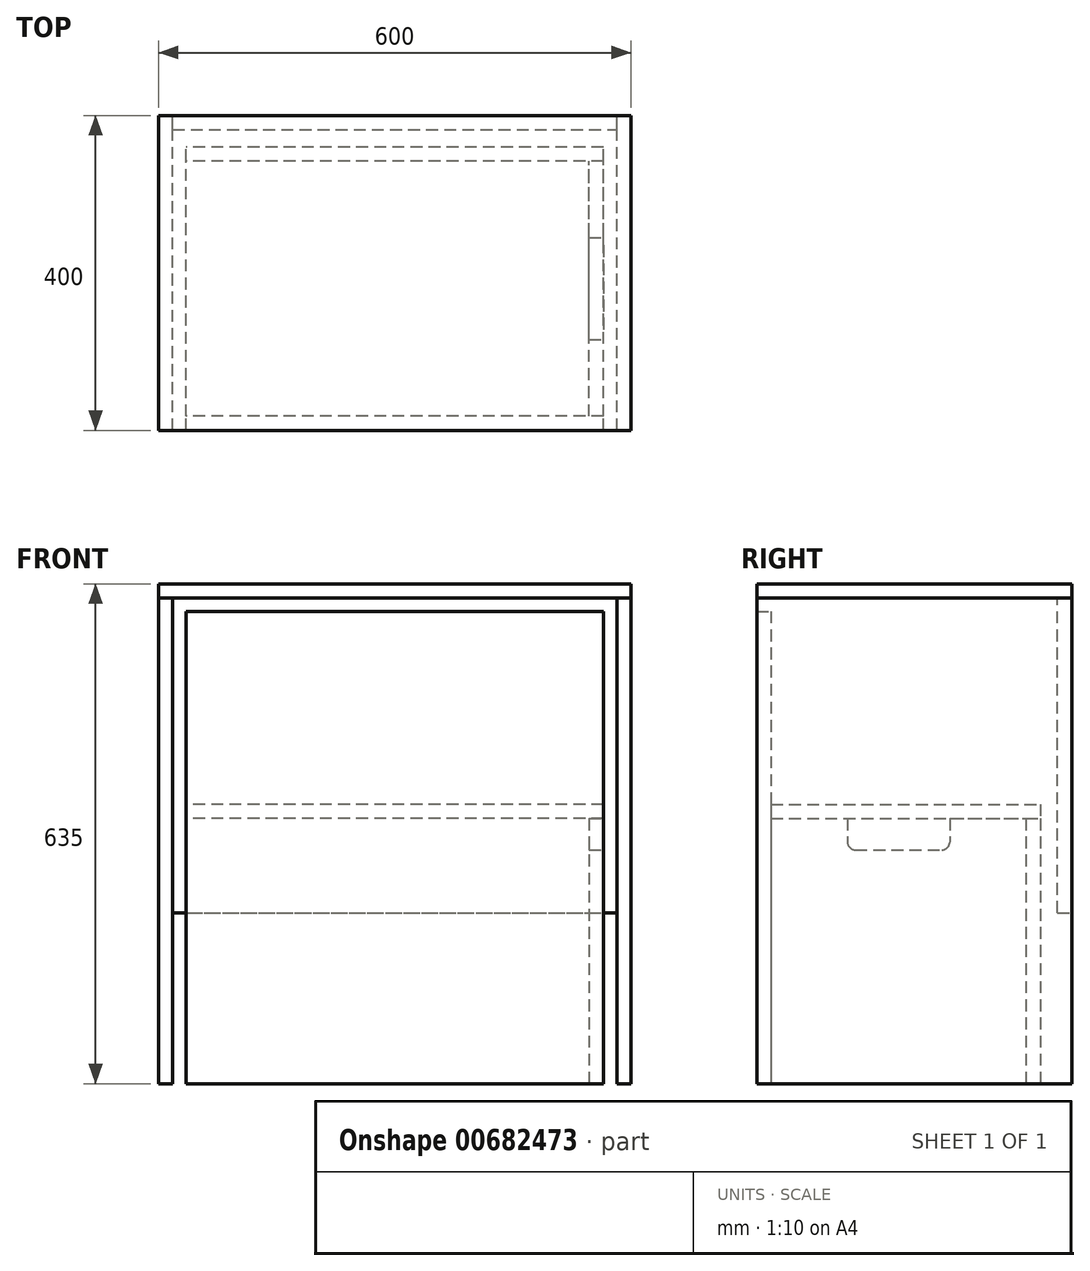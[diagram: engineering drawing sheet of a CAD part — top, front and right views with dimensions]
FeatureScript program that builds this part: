
annotation { "Feature Type Name" : "Feature", "Feature Type Description" : "" }
export const myFeature = defineFeature(function(context is Context, id is Id, definition is map)
    precondition{}
    {
        {
            var Q0;
            Q0=qCreatedBy(makeId("Front.planeOp"),FACE);
            var sketch = newSketch(context, id + "F0", { "sketchPlane" : qUnion([Q0])});
            skLineSegment(sketch, "E0.bottom", {"start": v(282, 0) * mm, "end": v(300, 0) * mm});
            skLineSegment(sketch, "E0.top", {"start": v(282, 617) * mm, "end": v(300, 617) * mm});
            skLineSegment(sketch, "E0.left", {"start": v(282, 0) * mm, "end": v(282, 617) * mm});
            skLineSegment(sketch, "E0.right", {"start": v(300, 0) * mm, "end": v(300, 617) * mm});
            skLineSegment(sketch, "E1.MirrorCS", {"start": v(-282, 0) * mm, "end": v(-282, 617) * mm});
            skLineSegment(sketch, "E2.MirrorCS", {"start": v(-282, 0) * mm, "end": v(-300, 0) * mm});
            skLineSegment(sketch, "E3.MirrorCS", {"start": v(-282, 617) * mm, "end": v(-300, 617) * mm});
            skLineSegment(sketch, "E4.MirrorCS", {"start": v(-300, 0) * mm, "end": v(-300, 617) * mm});
            skLineSegment(sketch, "E5.bottom", {"start": v(300, 617) * mm, "end": v(-300, 617) * mm});
            skLineSegment(sketch, "E5.top", {"start": v(300, 635) * mm, "end": v(-300, 635) * mm});
            skLineSegment(sketch, "E5.left", {"start": v(300, 617) * mm, "end": v(300, 635) * mm});
            skLineSegment(sketch, "E5.right", {"start": v(-300, 617) * mm, "end": v(-300, 635) * mm});
            skLineSegment(sketch, "E6", {"start": v(-282, 217) * mm, "end": v(282, 217) * mm});
            skSolve(sketch);
        }
        {
            var Q0;
            {var subQ1=sQuery(id+"F0.wireOp",EDGE,"E2.MirrorCS");Q0=makeQuery(id+"F0.imprint","IMPRINT",FACE,{"disambiguationData":[TD([[makeQuery(id+"F0.imprint","IMPRINT",EDGE,{"derivedFrom":subQ1}),-1.0]])]});}
            extrude(context, id + "F1", {"entities" : qUnion([Q0]), "depth" : 400 * mm, "offsetDistance" : 25 * mm});
        }
        {
            var Q0;
            {var subQ5=sQuery(id+"F0.wireOp",EDGE,"E0.bottom");Q0=makeQuery(id+"F0.imprint","IMPRINT",FACE,{"disambiguationData":[TD([[makeQuery(id+"F0.imprint","IMPRINT",EDGE,{"derivedFrom":subQ5}),1.0]])]});}
            extrude(context, id + "F2", {"entities" : qUnion([Q0]), "depth" : 400 * mm, "offsetDistance" : 25 * mm});
        }
        {
            var Q0;
            Q0=makeQuery(id+"F0.imprint","IMPRINT",FACE,{"disambiguationData":[TD([[makeQuery(id+"F0.imprint","IMPRINT",EDGE,{"derivedFrom":sQuery(id+"F0.wireOp",EDGE,"E5.top")}),1.0]])]});
            extrude(context, id + "F3", {"entities" : qUnion([Q0]), "depth" : 400 * mm, "offsetDistance" : 25 * mm});
        }
        {
            var Q0;
            {var subQ3=sQuery(id+"F0.wireOp",EDGE,"E6");Q0=makeQuery(id+"F0.imprint","IMPRINT",FACE,{"disambiguationData":[TD([[makeQuery(id+"F0.imprint","IMPRINT",EDGE,{"derivedFrom":subQ3}),1.0]])]});}
            extrude(context, id + "F4", {"entities" : qUnion([Q0]), "depth" : 18 * mm, "offsetDistance" : 25 * mm});
        }
        {
            var Q0;
            Q0=qCreatedBy(makeId("Right.planeOp"),FACE);
            var sketch = newSketch(context, id + "F5", { "sketchPlane" : qUnion([Q0])});
            skLineSegment(sketch, "E7.bottom", {"start": v(-400, 600) * mm, "end": v(-40, 600) * mm});
            skLineSegment(sketch, "E7.top", {"start": v(-400, 0) * mm, "end": v(-40, 0) * mm});
            skLineSegment(sketch, "E7.left", {"start": v(-400, 600) * mm, "end": v(-400, 0) * mm});
            skLineSegment(sketch, "E7.right", {"start": v(-40, 600) * mm, "end": v(-40, 0) * mm});
            skLineSegment(sketch, "E8", {"start": v(-382, 600) * mm, "end": v(-382, 0) * mm});
            skLineSegment(sketch, "E9.bottom", {"start": v(-382, 355) * mm, "end": v(-40, 355) * mm});
            skLineSegment(sketch, "E9.top", {"start": v(-382, 337) * mm, "end": v(-40, 337) * mm});
            skLineSegment(sketch, "E9.left", {"start": v(-382, 355) * mm, "end": v(-382, 337) * mm});
            skLineSegment(sketch, "E9.right", {"start": v(-40, 355) * mm, "end": v(-40, 337) * mm});
            skLineSegment(sketch, "E10", {"start": v(-58, 337) * mm, "end": v(-58, 0) * mm});
            skLineSegment(sketch, "E11", {"start": v(-364, 337) * mm, "end": v(-364, 287) * mm});
            skLineSegment(sketch, "E12", {"start": v(-364, 287) * mm, "end": v(-382, 287) * mm});
            skSolve(sketch);
        }
        {
            var Q0;
            {var subQ4=sQuery(id+"F5.wireOp",EDGE,"E7.left");Q0=makeQuery(id+"F5.imprint","IMPRINT",FACE,{"disambiguationData":[TD([[makeQuery(id+"F5.imprint","IMPRINT",EDGE,{"derivedFrom":subQ4}),1.0]])]});}
            extrude(context, id + "F6", {"entities" : qUnion([Q0]), "endBound" : BoundingType.SYMMETRIC, "depth" : 530 * mm, "offsetDistance" : 25 * mm});
        }
        {
            var Q0;
            Q0=makeQuery(id+"F5.imprint","IMPRINT",FACE,{"disambiguationData":[TD([[makeQuery(id+"F5.imprint","IMPRINT",EDGE,{"derivedFrom":sQuery(id+"F5.wireOp",EDGE,"E9.bottom")}),-1.0]])]});
            extrude(context, id + "F7", {"entities" : qUnion([Q0]), "endBound" : BoundingType.SYMMETRIC, "depth" : 530 * mm, "offsetDistance" : 25 * mm});
        }
        {
            var Q0;
            {var subQ3=sQuery(id+"F5.wireOp",EDGE,"E10");Q0=makeQuery(id+"F5.imprint","IMPRINT",FACE,{"disambiguationData":[TD([[makeQuery(id+"F5.imprint","IMPRINT",EDGE,{"derivedFrom":subQ3}),1.0]])]});}
            extrude(context, id + "F8", {"entities" : qUnion([Q0]), "endBound" : BoundingType.SYMMETRIC, "depth" : 530 * mm, "offsetDistance" : 25 * mm});
        }
        {
            var Q0;
            {var subQ0=sQuery(id+"F5.wireOp",EDGE,"E10");Q0=makeQuery(id+"F5.imprint","IMPRINT",FACE,{"disambiguationData":[TD([[makeQuery(id+"F5.imprint","IMPRINT",EDGE,{"derivedFrom":subQ0}),-1.0]])]});}
            var Q1;
            {var subQ4=sQuery(id+"F5.wireOp",EDGE,"E11");Q1=makeQuery(id+"F5.imprint","IMPRINT",FACE,{"disambiguationData":[TD([[makeQuery(id+"F5.imprint","IMPRINT",EDGE,{"derivedFrom":subQ4}),-1.0]])]});}
            extrude(context, id + "F9", {"entities" : qUnion([Q0, Q1]), "depth" : 530 * mm / 2, "offsetDistance" : 25 * mm, "hasSecondDirection" : true, "secondDirectionOppositeDirection" : false, "secondDirectionDepth" : (265 - 18) * mm});
        }
        {
            var Q0;
            Q0=makeQuery(id+"F9.opExtrude","CAP_FACE",FACE,{"disambiguationData":[OSD([sQuery(id+"F5.wireOp",EDGE,"E7.top"),sQuery(id+"F5.wireOp",EDGE,"E8"),sQuery(id+"F5.wireOp",EDGE,"E9.top"),sQuery(id+"F5.wireOp",EDGE,"E10")])],"isStart":false});
            var sketch = newSketch(context, id + "F10", { "sketchPlane" : qUnion([Q0])});
            skLineSegment(sketch, "E13.bottom", {"start": v(-155, 297) * mm, "end": v(-285, 297) * mm});
            skLineSegment(sketch, "E13.top", {"start": v(-155, 377) * mm, "end": v(-285, 377) * mm});
            skLineSegment(sketch, "E13.left", {"start": v(-155, 297) * mm, "end": v(-155, 377) * mm});
            skLineSegment(sketch, "E13.right", {"start": v(-285, 297) * mm, "end": v(-285, 377) * mm});
            skPoint(sketch, "E13.middle", {"position": v(-220, 337) * mm});
            skSolve(sketch);
        }
        {
            var Q0;
            {var subQ0=sQuery(id+"F10.wireOp",EDGE,"E13.bottom");Q0=makeQuery(id+"F10.imprint","IMPRINT",FACE,{"disambiguationData":[TD([[makeQuery(id+"F10.imprint","IMPRINT",EDGE,{"derivedFrom":subQ0}),-1.0]])]});}
            extrude(context, id + "F11", {"entities" : qUnion([Q0]), "operationType" : NewBodyOperationType.REMOVE, "endBound" : BoundingType.UP_TO_NEXT, "oppositeDirection" : true, "depth" : 25 * mm, "offsetDistance" : 25 * mm});
        }
        {
            var Q0;
            Q0=makeQuery(id+"F11.boolean.opBoolean","COPY",EDGE,{"derivedFrom":makeQuery(id+"F11.opExtrude","SWEPT_EDGE",EDGE,{"disambiguationData":[OSD([sQuery(id+"F10.wireOp",EDGE,"E13.bottom"),sQuery(id+"F10.wireOp",EDGE,"E13.right")])]})});
            var Q1;
            Q1=makeQuery(id+"F11.boolean.opBoolean","COPY",EDGE,{"derivedFrom":makeQuery(id+"F11.opExtrude","SWEPT_EDGE",EDGE,{"disambiguationData":[OSD([sQuery(id+"F10.wireOp",EDGE,"E13.bottom"),sQuery(id+"F10.wireOp",EDGE,"E13.left")])]})});
            fillet(context, id + "F12", {"entities" : qUnion([Q0, Q1]), "radius" : 10 * mm, "tangentPropagation" : true, "allowEdgeOverflow" : false});
        }
    });
